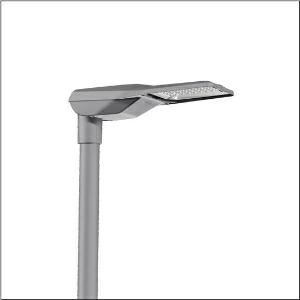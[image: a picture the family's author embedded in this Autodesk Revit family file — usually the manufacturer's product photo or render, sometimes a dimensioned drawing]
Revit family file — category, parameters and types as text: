
# Revit family: streetlight_sl_21_mini___st0_8a_5xe6c23a08hb_e2b8
name_source: partatom
category: Lighting Fixtures
units: mm (PartAtom-declared; Revit-internal decimal feet)

## family parameters
Cut with Voids When Loaded = No
Host = Face
Light Source = No
Part Type = Normal
Room Calculation Point = No
Round Connector Dimension = Use Diameter
Shared = No

## types (1)
- --- (1 x LED, 7490 lm, 66 W, 2200K)
    Apparent Load = 66 VA
    CIE Flux Codes = 38 75 97 100 100
    Color Rendering = 70
    Color Temperature = 2200K
    Default Elevation = 1800 mm
    Description = Streetlight SL 21 mini, mast luminaire, primary light control with lens, of PMMA, primary optical cover: cover, of toughened safety glass, transparent, light distribution: ST0.8a, light emission: direct distribution, primary light characteristic: asymmetric, installation type: post-top, side-entry, LED, 3G 1.5mm², High Power LED, rated luminous flux: 7.490lm, luminous efficacy: 114lm/W, light colour: 722, colour temperature: 2200K, control: overheat protection, constant luminous flux control, time-dependent luminous flux control, flexible luminous flux parameterisation, mains connection: 230..240V, AC, 50/60Hz, connection cable pre-assembled, cable length: 8,5m, wiring characteristics: H07RN-F, start of lifetime: 66W, end of service life: 69W, reduction: 30W, luminaire housing, of diecast aluminium, powder-coated, Siteco® metallic grey (DB 702S), corrosivity category C5 mid according to DIN EN ISO 12944, please order mast flange separately, inclination adjustable: 0°, 5°, 10°, 15°, sealing non-destructively replaceable, multi-level sealing system, length: 628mm, width: 235mm, height: 110mm, mast flange for spigot size: 42mm (side-entry): 5XC10008XM4, 60/48mm (side-entry/post-top): 5XC10108XM2, 76/60mm (side-entry/post-top): 5XC10108XM1, protection rating (complete): IP66, insulation class (complete): insulation class II (safety insulation), certification: CE, ENEC, ENEC+, VDE, impact resistance: IK09, permissible operating ambient temperature for outdoor applications: -40..+50°C, standard-compliant lighting for roads and squares, packaging unit: 1 piece

Light Distribution: ST0.8a
    Height = 110 mm
    Lamp = 1 x LED
    Lamp Light Flux = 7490 lm
    Lamp Power = 66 W
    Lamp count = 1
    Length = 625 mm
    Luminous efficacy = 113 lm/W
    Manufacturer = Siteco
    ModVariant = No
    Model = 5XE6C23A08HB
    Number of Poles = 1
    OnlyDefault = Yes
    Power Factor = 1
    Product Name = Streetlight SL 21 mini | ST0.8a
    Product group = mast luminaire | pylon top
    ProductGroupID = 6100
    Protection Class = Protection class II
    Protection Degree = IP 66
    RLX_Detail_Level = 1
    RLX_Emergency_Light_Flux = 0 lm
    RLX_Emergency_Type = 0
    RLX_Emergency_Type_DB = No
    RlxData = <blob elided: 93525 chars, md5=1a141db6>
    Socket = socket
    Standby Power = 0 W
    System Light Flux = 7490 lm
    System Power = 66 W
    Type Comments = factory setting: luminous flux: 100 % | Output Level: 100 % | 670 mA
    Type Image = l_1003519.jpg
    URL = http://relux.com
    VarID = @adj_136727
    Voltage = 0 V
    Weight = 0.00 kg
    Width = 234 mm

## geometry (parser evidence)
native form markers: Blend x4, Sweep x9
no freeform markers — native parametric forms only
